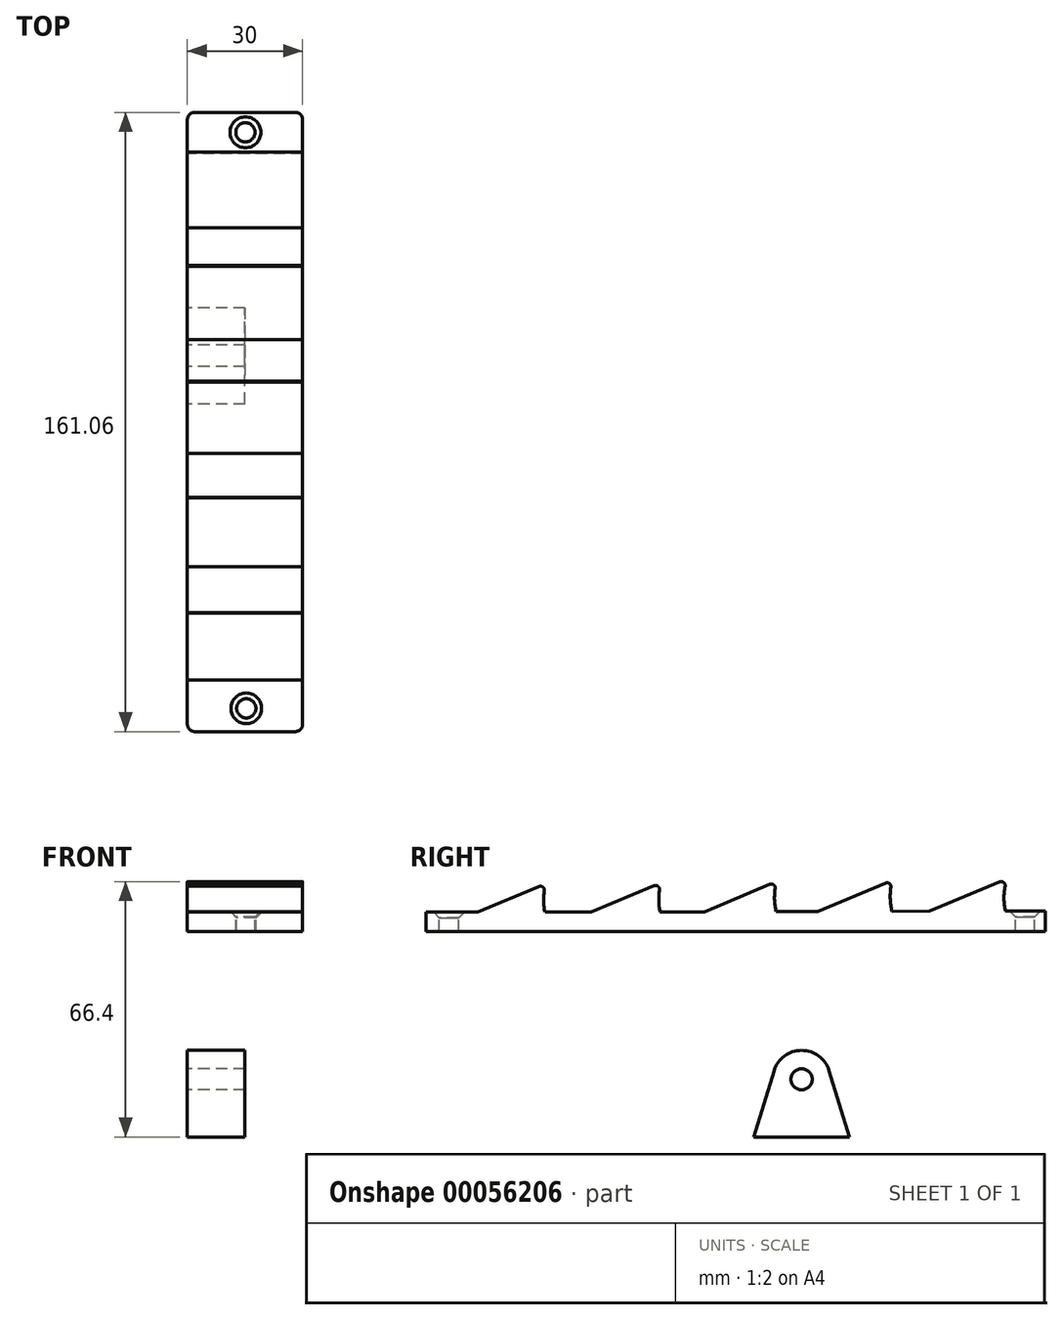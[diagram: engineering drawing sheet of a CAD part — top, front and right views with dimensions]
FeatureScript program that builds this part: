
annotation { "Feature Type Name" : "Feature", "Feature Type Description" : "" }
export const myFeature = defineFeature(function(context is Context, id is Id, definition is map)
    precondition{}
    {
        {
            var Q0;
            Q0=qCreatedBy(makeId("Right.planeOp"),FACE);
            var sketch = newSketch(context, id + "F0", { "sketchPlane" : qUnion([Q0])});
            skLineSegment(sketch, "E0", {"start": v(-103.28, 1.64) * mm, "end": v(36.72, 1.64) * mm});
            skLineSegment(sketch, "E1", {"start": v(-100.86, 6.61) * mm, "end": v(-83.13, 14.02) * mm});
            skArc(sketch, "E2", {"start": v(-83.13, 14.02) * mm, "mid": v(-83.67, 10.33) * mm, "end": v(-83.34, 6.61) * mm});
            skLineSegment(sketch, "E3", {"start": v(-71.4, 6.64) * mm, "end": v(-53.2, 14.24) * mm});
            skArc(sketch, "E4", {"start": v(-53.2, 14.24) * mm, "mid": v(-53.75, 10.48) * mm, "end": v(-53.39, 6.7) * mm});
            skLineSegment(sketch, "E5", {"start": v(-41.93, 6.72) * mm, "end": v(-23.12, 14.58) * mm});
            skArc(sketch, "E6", {"start": v(-23.12, 14.58) * mm, "mid": v(-23.66, 10.68) * mm, "end": v(-23.24, 6.77) * mm});
            skLineSegment(sketch, "E7", {"start": v(-12.46, 6.8) * mm, "end": v(6.97, 14.92) * mm});
            skArc(sketch, "E8", {"start": v(6.97, 14.92) * mm, "mid": v(6.43, 10.9) * mm, "end": v(6.92, 6.86) * mm});
            skLineSegment(sketch, "E9", {"start": v(16.72, 6.88) * mm, "end": v(36.78, 15.26) * mm});
            skArc(sketch, "E10", {"start": v(36.78, 15.26) * mm, "mid": v(36.03, 11.1) * mm, "end": v(36.39, 6.88) * mm});
            skLineSegment(sketch, "E11", {"start": v(36.72, 1.64) * mm, "end": v(46.72, 1.64) * mm});
            skLineSegment(sketch, "E12", {"start": v(46.72, 1.64) * mm, "end": v(46.72, 5.64) * mm});
            skLineSegment(sketch, "E13", {"start": v(6.92, 6.86) * mm, "end": v(16.72, 6.88) * mm});
            skLineSegment(sketch, "E14", {"start": v(16.72, 6.88) * mm, "end": v(6.92, 6.86) * mm});
            skPoint(sketch, "E15.orphan", {"position": v(-13.08, 6.54) * mm});
            skPoint(sketch, "E16.orphan", {"position": v(-23.18, 6.52) * mm});
            skLineSegment(sketch, "E17.trimOffspring", {"start": v(-12.46, 6.8) * mm, "end": v(-23.24, 6.77) * mm});
            skLineSegment(sketch, "E18.trimOffspring", {"start": v(-41.93, 6.72) * mm, "end": v(-53.39, 6.7) * mm});
            skPoint(sketch, "E19.orphan", {"position": v(-53.27, 6.18) * mm});
            skPoint(sketch, "E20.orphan", {"position": v(-43.18, 6.2) * mm});
            skLineSegment(sketch, "E21.trimOffspring", {"start": v(-71.4, 6.64) * mm, "end": v(-83.34, 6.61) * mm});
            skPoint(sketch, "E22.orphan", {"position": v(-73.27, 5.86) * mm});
            skPoint(sketch, "E23.orphan", {"position": v(-83.2, 5.95) * mm});
            skLineSegment(sketch, "E24", {"start": v(36.39, 6.88) * mm, "end": v(46.72, 6.88) * mm});
            skPoint(sketch, "E25.orphan", {"position": v(36.72, 5.64) * mm});
            skLineSegment(sketch, "E26", {"start": v(46.72, 5.64) * mm, "end": v(46.72, 6.88) * mm});
            skLineSegment(sketch, "E27.top", {"start": v(-103.2, 1.64) * mm, "end": v(-103.28, 1.64) * mm});
            skLineSegment(sketch, "E28", {"start": v(-100.86, 6.61) * mm, "end": v(-114.34, 6.61) * mm});
            skLineSegment(sketch, "E29", {"start": v(-114.34, 6.61) * mm, "end": v(-114.34, 1.64) * mm});
            skPoint(sketch, "E27.right.end.orphan", {"position": v(-110.77, 1.64) * mm});
            skPoint(sketch, "E30.orphan", {"position": v(-103.2, 5.64) * mm});
            skLineSegment(sketch, "E31", {"start": v(-103.2, 1.64) * mm, "end": v(-114.34, 1.64) * mm});
            skSolve(sketch);
        }
        {
            var Q0;
            Q0=qSketchRegion(id+"F0",true);
            var Q1;
            Q1=sQuery(id+"F0.wireOp",EDGE,"E0");
            var Q2;
            Q2=sQuery(id+"F0.wireOp",EDGE,"E1");
            var Q3;
            Q3=sQuery(id+"F0.wireOp",EDGE,"E2");
            var Q4;
            Q4=sQuery(id+"F0.wireOp",EDGE,"aVXR79yY-1hjt-y3u3-m6eV-zaEhtOIxPnFv");
            var Q5;
            Q5=sQuery(id+"F0.wireOp",EDGE,"4554b6e0-54a2-462e-aa4e-58822ef9da20");
            var Q6;
            Q6=sQuery(id+"F0.wireOp",EDGE,"E3");
            var Q7;
            Q7=sQuery(id+"F0.wireOp",EDGE,"E4");
            var Q8;
            Q8=sQuery(id+"F0.wireOp",EDGE,"a5485bb7-b8e9-40f3-8546-a96ed6ddff3a");
            var Q9;
            Q9=sQuery(id+"F0.wireOp",EDGE,"E5");
            var Q10;
            Q10=sQuery(id+"F0.wireOp",EDGE,"E6");
            var Q11;
            Q11=sQuery(id+"F0.wireOp",EDGE,"a28d2f95-e289-46cd-9a1f-94b747a0afc5");
            var Q12;
            Q12=sQuery(id+"F0.wireOp",EDGE,"E7");
            var Q13;
            Q13=sQuery(id+"F0.wireOp",EDGE,"E8");
            var Q14;
            Q14=sQuery(id+"F0.wireOp",EDGE,"E12");
            var Q15;
            Q15=sQuery(id+"F0.wireOp",EDGE,"ae9abd8c-4da3-48e8-ab53-a4a2666a44f8");
            var Q16;
            Q16=sQuery(id+"F0.wireOp",EDGE,"E11");
            var Q17;
            Q17=sQuery(id+"F0.wireOp",EDGE,"E9");
            var Q18;
            Q18=sQuery(id+"F0.wireOp",EDGE,"E10");
            var Q19;
            Q19=sQuery(id+"F0.wireOp",EDGE,"KTlvuNxW-LSAw-ywOI-KxQU-ba1FE6igpGGa");
            extrude(context, id + "F1", {"entities" : qUnion([Q0]), "surfaceEntities" : qUnion([Q1, Q2, Q3, Q4, Q5, Q6, Q7, Q8, Q9, Q10, Q11, Q12, Q13, Q14, Q15, Q16, Q17, Q18, Q19]), "depth" : 30 * mm});
        }
        {
            var Q0;
            Q0=makeQuery(id+"F1.opExtrude","CAP_EDGE",EDGE,{"disambiguationData":[OSD([sQuery(id+"F0.wireOp",EDGE,"E29")])],"isStart":true});
            var Q1;
            Q1=makeQuery(id+"F1.opExtrude","CAP_EDGE",EDGE,{"disambiguationData":[OSD([sQuery(id+"F0.wireOp",EDGE,"E29")])],"isStart":false});
            var Q2;
            Q2=makeQuery(id+"F1.opExtrude","CAP_EDGE",EDGE,{"disambiguationData":[OSD([sQuery(id+"F0.wireOp",EDGE,"E12"),sQuery(id+"F0.wireOp",EDGE,"E26")])],"isStart":true});
            var Q3;
            Q3=makeQuery(id+"F1.opExtrude","CAP_EDGE",EDGE,{"disambiguationData":[OSD([sQuery(id+"F0.wireOp",EDGE,"E12"),sQuery(id+"F0.wireOp",EDGE,"E26")])],"isStart":false});
            fillet(context, id + "F2", {"entities" : qUnion([Q0, Q1, Q2, Q3]), "radius" : 2 * mm, "tangentPropagation" : true, "allowEdgeOverflow" : false});
        }
        {
            var Q0;
            Q0=makeQuery(id+"F1.opExtrude","SWEPT_EDGE",EDGE,{"disambiguationData":[OSD([sQuery(id+"F0.wireOp",EDGE,"E9"),sQuery(id+"F0.wireOp",EDGE,"E10")])]});
            var Q1;
            Q1=makeQuery(id+"F1.opExtrude","SWEPT_EDGE",EDGE,{"disambiguationData":[OSD([sQuery(id+"F0.wireOp",EDGE,"E7"),sQuery(id+"F0.wireOp",EDGE,"E8")])]});
            var Q2;
            Q2=makeQuery(id+"F1.opExtrude","SWEPT_EDGE",EDGE,{"disambiguationData":[OSD([sQuery(id+"F0.wireOp",EDGE,"E5"),sQuery(id+"F0.wireOp",EDGE,"E6")])]});
            var Q3;
            Q3=makeQuery(id+"F1.opExtrude","SWEPT_EDGE",EDGE,{"disambiguationData":[OSD([sQuery(id+"F0.wireOp",EDGE,"E3"),sQuery(id+"F0.wireOp",EDGE,"E4")])]});
            var Q4;
            Q4=makeQuery(id+"F1.opExtrude","SWEPT_EDGE",EDGE,{"disambiguationData":[OSD([sQuery(id+"F0.wireOp",EDGE,"E1"),sQuery(id+"F0.wireOp",EDGE,"E2")])]});
            fillet(context, id + "F3", {"entities" : qUnion([Q0, Q1, Q2, Q3, Q4]), "radius" : 1 * mm, "tangentPropagation" : true, "allowEdgeOverflow" : false});
        }
        {
            var Q0;
            Q0=makeQuery(id+"F1.opExtrude","SWEPT_FACE",FACE,{"disambiguationData":[OSD([sQuery(id+"F0.wireOp",EDGE,"E28")])]});
            var sketch = newSketch(context, id + "F4", { "sketchPlane" : qUnion([Q0])});
            skPoint(sketch, "E32", {"position": v(15.34, -108.28) * mm});
            skPoint(sketch, "E33", {"position": v(161.37, -142.1) * mm});
            skSolve(sketch);
        }
        {
            var Q0;
            Q0=sQuery(id+"F4.wireOp",VERTEX,"E32");
            var Q1;
            Q1=makeQuery(id+"F1.opExtrude","SWEPT_BODY",BODY,{"disambiguationData":[OSD([sQuery(id+"F0.wireOp",EDGE,"E0"),sQuery(id+"F0.wireOp",EDGE,"E1"),sQuery(id+"F0.wireOp",EDGE,"E2"),sQuery(id+"F0.wireOp",EDGE,"E3"),sQuery(id+"F0.wireOp",EDGE,"E4"),sQuery(id+"F0.wireOp",EDGE,"E5"),sQuery(id+"F0.wireOp",EDGE,"E6"),sQuery(id+"F0.wireOp",EDGE,"E7"),sQuery(id+"F0.wireOp",EDGE,"E8"),sQuery(id+"F0.wireOp",EDGE,"E9"),sQuery(id+"F0.wireOp",EDGE,"E10"),sQuery(id+"F0.wireOp",EDGE,"E11"),sQuery(id+"F0.wireOp",EDGE,"E12"),sQuery(id+"F0.wireOp",EDGE,"E14"),sQuery(id+"F0.wireOp",EDGE,"E17.trimOffspring"),sQuery(id+"F0.wireOp",EDGE,"E18.trimOffspring"),sQuery(id+"F0.wireOp",EDGE,"E21.trimOffspring"),sQuery(id+"F0.wireOp",EDGE,"E24"),sQuery(id+"F0.wireOp",EDGE,"E26"),sQuery(id+"F0.wireOp",EDGE,"E28"),sQuery(id+"F0.wireOp",EDGE,"E29"),sQuery(id+"F0.wireOp",EDGE,"E31")])]});
            hole(context, id + "F5", {"style" : HoleStyle.C_SINK, "holeDiameter" : 5 * mm, "cSinkDiameter" : 8 * mm, "endStyle" : HoleEndStyle.THROUGH, "locations" : qUnion([Q0]), "scope" : qUnion([Q1]), "cSinkAngle" : 90 * degree});
        }
        {
            var Q0;
            Q0=makeQuery(id+"F1.opExtrude","SWEPT_FACE",FACE,{"disambiguationData":[OSD([sQuery(id+"F0.wireOp",EDGE,"E24")])]});
            var sketch = newSketch(context, id + "F6", { "sketchPlane" : qUnion([Q0])});
            skPoint(sketch, "E34", {"position": v(15.11, 41.5) * mm});
            skSolve(sketch);
        }
        {
            var Q0;
            Q0=sQuery(id+"F6.wireOp",VERTEX,"E34");
            var Q1;
            Q1=makeQuery(id+"F1.opExtrude","SWEPT_BODY",BODY,{"disambiguationData":[OSD([sQuery(id+"F0.wireOp",EDGE,"E0"),sQuery(id+"F0.wireOp",EDGE,"E1"),sQuery(id+"F0.wireOp",EDGE,"E2"),sQuery(id+"F0.wireOp",EDGE,"E3"),sQuery(id+"F0.wireOp",EDGE,"E4"),sQuery(id+"F0.wireOp",EDGE,"E5"),sQuery(id+"F0.wireOp",EDGE,"E6"),sQuery(id+"F0.wireOp",EDGE,"E7"),sQuery(id+"F0.wireOp",EDGE,"E8"),sQuery(id+"F0.wireOp",EDGE,"E9"),sQuery(id+"F0.wireOp",EDGE,"E10"),sQuery(id+"F0.wireOp",EDGE,"E11"),sQuery(id+"F0.wireOp",EDGE,"E12"),sQuery(id+"F0.wireOp",EDGE,"E14"),sQuery(id+"F0.wireOp",EDGE,"E17.trimOffspring"),sQuery(id+"F0.wireOp",EDGE,"E18.trimOffspring"),sQuery(id+"F0.wireOp",EDGE,"E21.trimOffspring"),sQuery(id+"F0.wireOp",EDGE,"E24"),sQuery(id+"F0.wireOp",EDGE,"E26"),sQuery(id+"F0.wireOp",EDGE,"E28"),sQuery(id+"F0.wireOp",EDGE,"E29"),sQuery(id+"F0.wireOp",EDGE,"E31")])]});
            hole(context, id + "F7", {"style" : HoleStyle.C_SINK, "holeDiameter" : 5 * mm, "cSinkDiameter" : 8 * mm, "endStyle" : HoleEndStyle.THROUGH, "locations" : qUnion([Q0]), "scope" : qUnion([Q1]), "cSinkAngle" : 90 * degree});
        }
        {
            var Q0;
            Q0=qCreatedBy(makeId("Right.planeOp"),FACE);
            var sketch = newSketch(context, id + "F8", { "sketchPlane" : qUnion([Q0])});
            skCircle(sketch, "E35", {"center": v(-16.6, -36.83) * mm, "radius": 2.75 * mm});
            skArc(sketch, "E36", {"start": v(-9.44, -34.61) * mm, "mid": v(-16.6, -29.33) * mm, "end": v(-23.77, -34.61) * mm});
            skLineSegment(sketch, "E37", {"start": v(-29.1, -51.83) * mm, "end": v(-4.1, -51.83) * mm});
            skLineSegment(sketch, "E38", {"start": v(-29.1, -51.83) * mm, "end": v(-23.77, -34.61) * mm});
            skLineSegment(sketch, "E39", {"start": v(-4.1, -51.83) * mm, "end": v(-9.44, -34.61) * mm});
            skPoint(sketch, "E40.orphan", {"position": v(-16.6, -51.83) * mm});
            skSolve(sketch);
        }
        {
            var Q0;
            Q0 = qSketchRegion(id + "F8", true);
            extrude(context, id + "F9", {"entities" : qUnion([Q0]), "depth" : 15 * mm});
        }
    });
